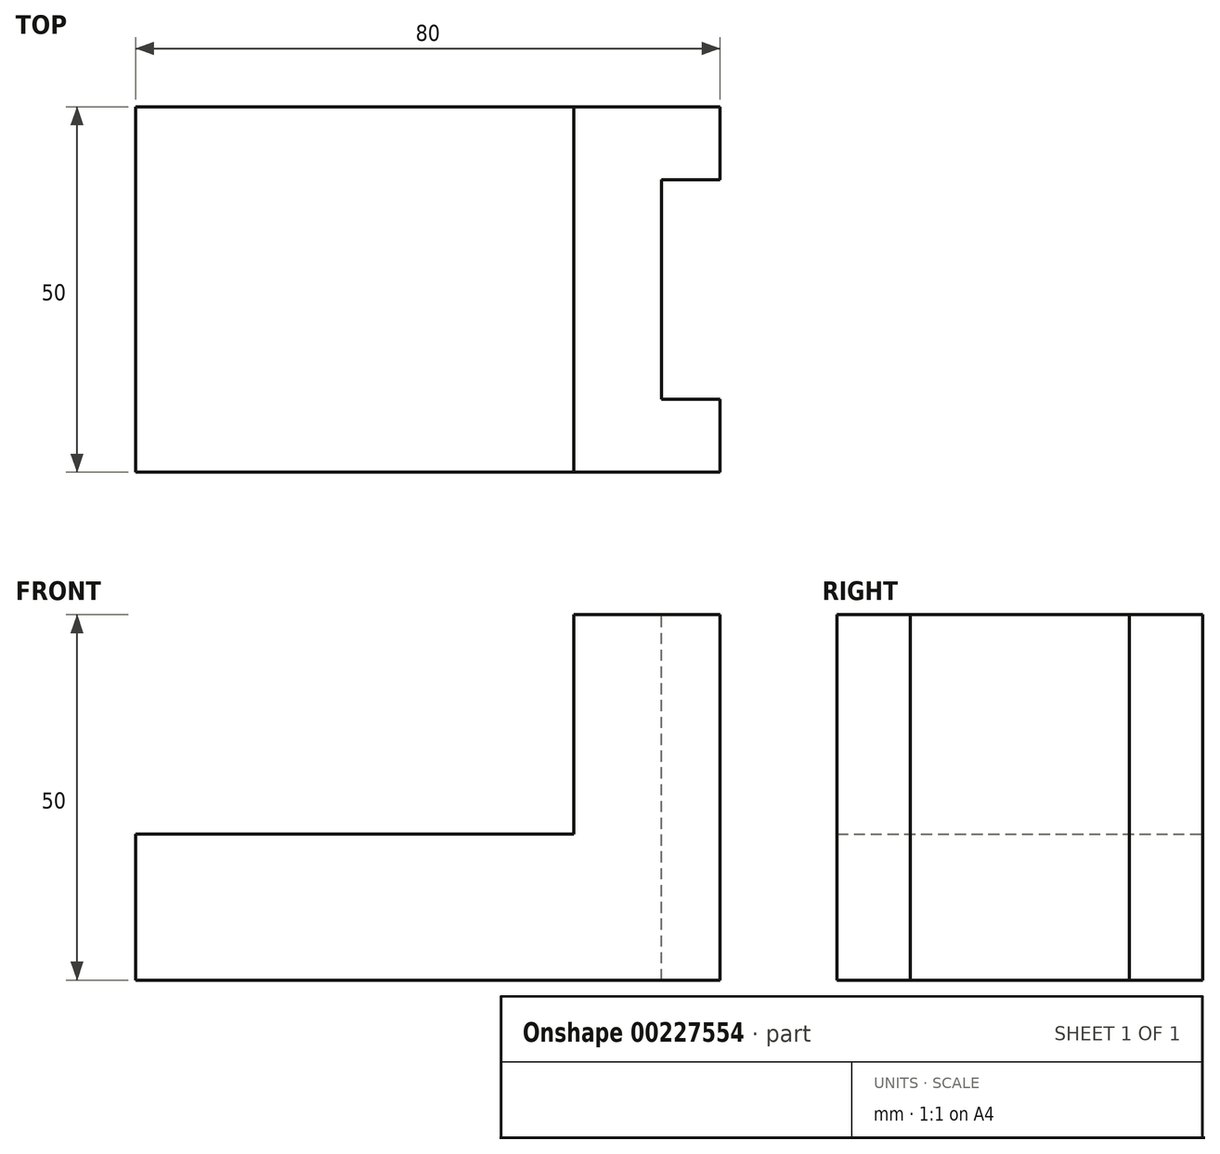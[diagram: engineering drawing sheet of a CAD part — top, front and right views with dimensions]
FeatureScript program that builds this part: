
annotation { "Feature Type Name" : "Feature", "Feature Type Description" : "" }
export const myFeature = defineFeature(function(context is Context, id is Id, definition is map)
    precondition{}
    {
        {
            var Q0;
            Q0=qCreatedBy(makeId("Front.planeOp"),FACE);
            var sketch = newSketch(context, id + "F0", { "sketchPlane" : qUnion([Q0])});
            skLineSegment(sketch, "E0", {"start": v(-48.26, -7.9) * mm, "end": v(11.74, -7.9) * mm});
            skLineSegment(sketch, "E1", {"start": v(11.74, -7.9) * mm, "end": v(11.74, 22.1) * mm});
            skLineSegment(sketch, "E2", {"start": v(11.74, 22.1) * mm, "end": v(31.74, 22.1) * mm});
            skLineSegment(sketch, "E3", {"start": v(31.74, 22.1) * mm, "end": v(31.74, -27.9) * mm});
            skLineSegment(sketch, "E4", {"start": v(31.74, -27.9) * mm, "end": v(-48.26, -27.9) * mm});
            skLineSegment(sketch, "E5", {"start": v(-48.26, -27.9) * mm, "end": v(-48.26, -7.9) * mm});
            skSolve(sketch);
        }
        {
            var Q0;
            Q0 = qSketchRegion(id + "F0", true);
            extrude(context, id + "F1", {"entities" : qUnion([Q0]), "depth" : 50 * mm});
        }
        {
            var Q0;
            Q0=makeQuery(id+"F1.opExtrude","SWEPT_FACE",FACE,{"disambiguationData":[OSD([sQuery(id+"F0.wireOp",EDGE,"E2")])]});
            var sketch = newSketch(context, id + "F2", { "sketchPlane" : qUnion([Q0])});
            skLineSegment(sketch, "E6.0", {"start": v(11.74, -50) * mm, "end": v(11.74, 0) * mm, "construction": true});
            skLineSegment(sketch, "E6.1", {"start": v(31.74, -50) * mm, "end": v(31.74, 0) * mm, "construction": true});
            skLineSegment(sketch, "E6.2", {"start": v(-48.26, 0) * mm, "end": v(11.74, 0) * mm, "construction": true});
            skLineSegment(sketch, "E6.4", {"start": v(11.74, 0) * mm, "end": v(31.74, 0) * mm, "construction": true});
            skLineSegment(sketch, "E6.5", {"start": v(11.74, -50) * mm, "end": v(11.74, 0) * mm, "construction": true});
            skLineSegment(sketch, "E6.6", {"start": v(31.74, 0) * mm, "end": v(-48.26, 0) * mm, "construction": true});
            skLineSegment(sketch, "E6.7", {"start": v(31.74, -50) * mm, "end": v(31.74, 0) * mm, "construction": true});
            skLineSegment(sketch, "E7.0", {"start": v(11.74, -50) * mm, "end": v(31.74, -50) * mm, "construction": true});
            skLineSegment(sketch, "E7.1", {"start": v(31.74, -50) * mm, "end": v(-48.26, -50) * mm, "construction": true});
            skLineSegment(sketch, "E8", {"start": v(31.74, -10) * mm, "end": v(23.74, -10) * mm});
            skLineSegment(sketch, "E9", {"start": v(23.74, -10) * mm, "end": v(23.74, -40) * mm});
            skLineSegment(sketch, "E10", {"start": v(23.74, -40) * mm, "end": v(31.74, -40) * mm});
            skLineSegment(sketch, "E11", {"start": v(31.74, -40) * mm, "end": v(31.74, -10) * mm});
            skSolve(sketch);
        }
        {
            var Q0;
            Q0=makeQuery(id+"F2.imprint","IMPRINT",FACE,{"disambiguationData":[TD([[makeQuery(id+"F2.imprint","IMPRINT",EDGE,{"derivedFrom":sQuery(id+"F2.wireOp",EDGE,"E8")}),1.0]])]});
            extrude(context, id + "F3", {"entities" : qUnion([Q0]), "operationType" : NewBodyOperationType.REMOVE, "oppositeDirection" : true, "depth" : 57.2 * mm});
        }
    });
